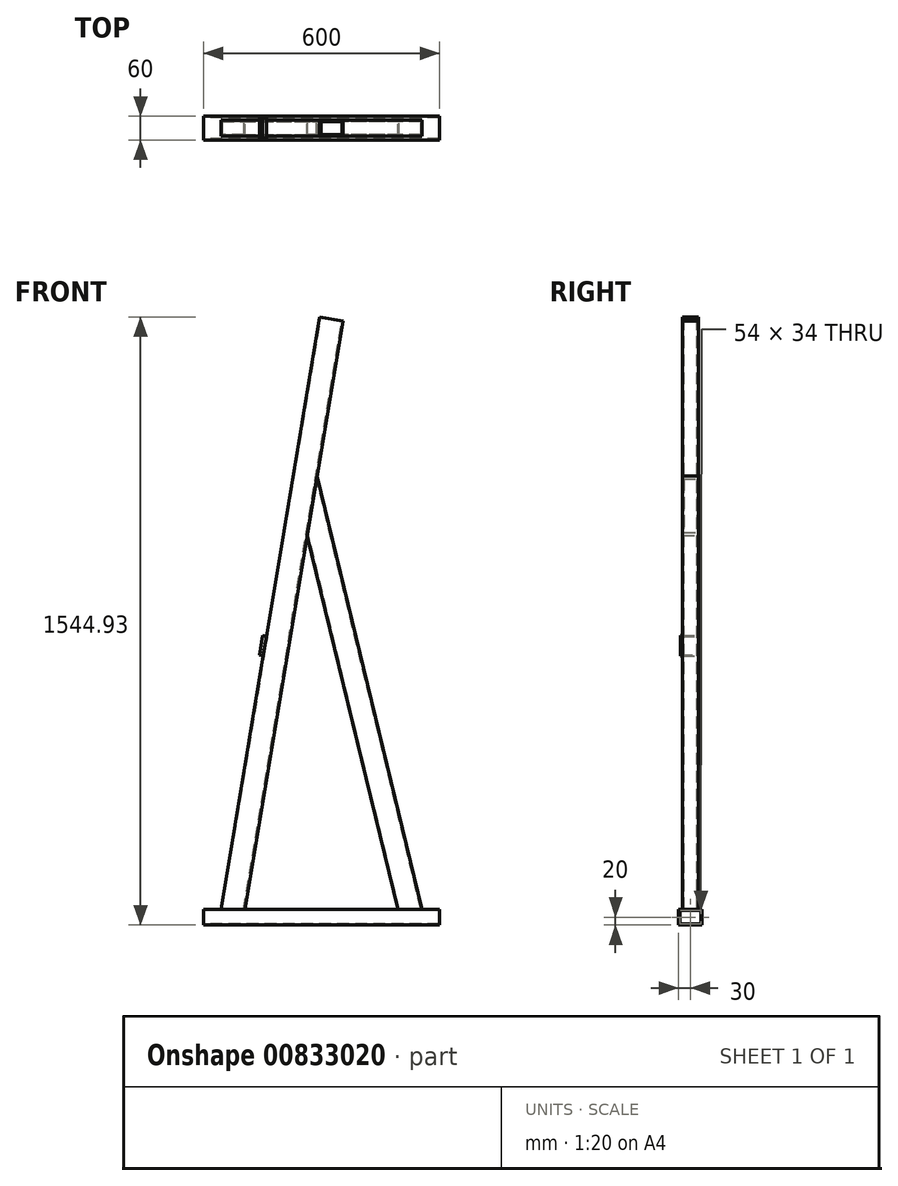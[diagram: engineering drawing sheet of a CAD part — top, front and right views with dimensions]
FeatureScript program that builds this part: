
annotation { "Feature Type Name" : "Feature", "Feature Type Description" : "" }
export const myFeature = defineFeature(function(context is Context, id is Id, definition is map)
    precondition{}
    {
        {
            var Q0;
            Q0=qCreatedBy(makeId("Front.planeOp"),FACE);
            var sketch = newSketch(context, id + "F0", { "sketchPlane" : qUnion([Q0])});
            skLineSegment(sketch, "E0", {"start": v(75, 0) * mm, "end": v(325, 1500) * mm});
            skLineSegment(sketch, "E1", {"start": v(258.33, 1100) * mm, "end": v(525, 0) * mm});
            skLineSegment(sketch, "E2", {"start": v(0, 0) * mm, "end": v(600, 0) * mm});
            skPoint(sketch, "E3", {"position": v(391.67, 550) * mm});
            skSolve(sketch);
        }
        {
            var Q0;
            Q0=sQuery(id+"F0.wireOp",EDGE,"E2");
            var Q1;
            Q1=sQuery(id+"F0.wireOp",VERTEX,"E2.end");
            cPlane(context, id + "F1", {"entities" : qUnion([Q0, Q1]), "cplaneType" : CPlaneType.LINE_POINT, "offset" : 25 * mm, "width" : 150 * mm, "height" : 150 * mm});
        }
        {
            var Q0;
            Q0=qCreatedBy(id+"F1.planeOp",FACE);
            var sketch = newSketch(context, id + "F2", { "sketchPlane" : qUnion([Q0])});
            skLineSegment(sketch, "E4.bottom", {"start": v(-30, 0) * mm, "end": v(30, 0) * mm});
            skLineSegment(sketch, "E4.top", {"start": v(-30, -40) * mm, "end": v(30, -40) * mm});
            skLineSegment(sketch, "E4.left", {"start": v(-30, 0) * mm, "end": v(-30, -40) * mm});
            skLineSegment(sketch, "E4.right", {"start": v(30, 0) * mm, "end": v(30, -40) * mm});
            skLineSegment(sketch, "E5", {"start": v(0, 0) * mm, "end": v(0, -40) * mm, "construction": true});
            skLineSegment(sketch, "E6", {"start": v(30, -20) * mm, "end": v(-30, -20) * mm, "construction": true});
            skLineSegment(sketch, "E7.bottom", {"start": v(27, -3) * mm, "end": v(-27, -3) * mm});
            skLineSegment(sketch, "E7.top", {"start": v(27, -37) * mm, "end": v(-27, -37) * mm});
            skLineSegment(sketch, "E7.left", {"start": v(27, -3) * mm, "end": v(27, -37) * mm});
            skLineSegment(sketch, "E7.right", {"start": v(-27, -3) * mm, "end": v(-27, -37) * mm});
            skSolve(sketch);
        }
        {
            var Q0;
            Q0=makeQuery(id+"F2.imprint","IMPRINT",FACE,{"disambiguationData":[TD([[makeQuery(id+"F2.imprint","IMPRINT",EDGE,{"derivedFrom":sQuery(id+"F2.wireOp",EDGE,"E4.bottom")}),-1.0]])]});
            var Q1;
            Q1=sQuery(id+"F0.wireOp",EDGE,"E2");
            sweep(context, id + "F3", {"profiles" : qUnion([Q0]), "path" : qUnion([Q1])});
        }
        {
            var Q0;
            Q0=sQuery(id+"F0.wireOp",EDGE,"E0");
            var Q1;
            Q1=sQuery(id+"F0.wireOp",VERTEX,"E0.end");
            cPlane(context, id + "F4", {"entities" : qUnion([Q0, Q1]), "cplaneType" : CPlaneType.LINE_POINT, "offset" : 25 * mm, "width" : 150 * mm, "height" : 150 * mm});
        }
        {
            var Q0;
            Q0=qCreatedBy(id+"F4.planeOp",FACE);
            var sketch = newSketch(context, id + "F5", { "sketchPlane" : qUnion([Q0])});
            skPoint(sketch, "E8.0", {"position": v(73.98, 0) * mm});
            skLineSegment(sketch, "E9.bottom", {"start": v(103.98, 20) * mm, "end": v(43.98, 20) * mm});
            skLineSegment(sketch, "E9.top", {"start": v(103.98, -20) * mm, "end": v(43.98, -20) * mm});
            skLineSegment(sketch, "E9.left", {"start": v(103.98, 20) * mm, "end": v(103.98, -20) * mm});
            skLineSegment(sketch, "E9.right", {"start": v(43.98, 20) * mm, "end": v(43.98, -20) * mm});
            skLineSegment(sketch, "E10.bottom", {"start": v(46.98, -17) * mm, "end": v(100.98, -17) * mm});
            skLineSegment(sketch, "E10.top", {"start": v(46.98, 17) * mm, "end": v(100.98, 17) * mm});
            skLineSegment(sketch, "E10.left", {"start": v(46.98, -17) * mm, "end": v(46.98, 17) * mm});
            skLineSegment(sketch, "E10.right", {"start": v(100.98, -17) * mm, "end": v(100.98, 17) * mm});
            skSolve(sketch);
        }
        {
            var Q0;
            Q0=makeQuery(id+"F5.imprint","IMPRINT",FACE,{"disambiguationData":[TD([[makeQuery(id+"F5.imprint","IMPRINT",EDGE,{"derivedFrom":sQuery(id+"F5.wireOp",EDGE,"E9.bottom")}),1.0]])]});
            var Q1;
            Q1=makeQuery(id+"F3.opSweep","SWEPT_BODY",BODY,{"disambiguationData":[OSD([sQuery(id+"F0.wireOp",EDGE,"E2"),sQuery(id+"F2.wireOp",EDGE,"E4.bottom"),sQuery(id+"F2.wireOp",EDGE,"E4.top"),sQuery(id+"F2.wireOp",EDGE,"E4.left"),sQuery(id+"F2.wireOp",EDGE,"E4.right"),sQuery(id+"F2.wireOp",EDGE,"E7.bottom"),sQuery(id+"F2.wireOp",EDGE,"E7.top"),sQuery(id+"F2.wireOp",EDGE,"E7.left"),sQuery(id+"F2.wireOp",EDGE,"E7.right")])]});
            extrude(context, id + "F6", {"entities" : qUnion([Q0]), "endBound" : BoundingType.UP_TO_BODY, "oppositeDirection" : true, "depth" : 25 * mm, "endBoundEntityBody" : qUnion([Q1]), "offsetDistance" : 25 * mm});
        }
        {
            var Q0;
            Q0=sQuery(id+"F0.wireOp",EDGE,"E1");
            var Q1;
            Q1=sQuery(id+"F0.wireOp",VERTEX,"E3");
            cPlane(context, id + "F7", {"entities" : qUnion([Q0, Q1]), "cplaneType" : CPlaneType.LINE_POINT, "offset" : 25 * mm, "width" : 150 * mm, "height" : 150 * mm});
        }
        {
            var Q0;
            Q0=qCreatedBy(id+"F7.planeOp",FACE);
            var sketch = newSketch(context, id + "F8", { "sketchPlane" : qUnion([Q0])});
            skPoint(sketch, "E11.0", {"position": v(510.22, 0) * mm});
            skLineSegment(sketch, "E12.bottom", {"start": v(480.22, -20) * mm, "end": v(540.22, -20) * mm});
            skLineSegment(sketch, "E12.top", {"start": v(480.22, 20) * mm, "end": v(540.22, 20) * mm});
            skLineSegment(sketch, "E12.left", {"start": v(480.22, -20) * mm, "end": v(480.22, 20) * mm});
            skLineSegment(sketch, "E12.right", {"start": v(540.22, -20) * mm, "end": v(540.22, 20) * mm});
            skLineSegment(sketch, "E13.bottom", {"start": v(483.22, -17) * mm, "end": v(537.22, -17) * mm});
            skLineSegment(sketch, "E13.top", {"start": v(483.22, 17) * mm, "end": v(537.22, 17) * mm});
            skLineSegment(sketch, "E13.left", {"start": v(483.22, -17) * mm, "end": v(483.22, 17) * mm});
            skLineSegment(sketch, "E13.right", {"start": v(537.22, -17) * mm, "end": v(537.22, 17) * mm});
            skSolve(sketch);
        }
        {
            var Q0;
            Q0=makeQuery(id+"F8.imprint","IMPRINT",FACE,{"disambiguationData":[TD([[makeQuery(id+"F8.imprint","IMPRINT",EDGE,{"derivedFrom":sQuery(id+"F8.wireOp",EDGE,"E12.bottom")}),1.0]])]});
            var Q1;
            Q1=makeQuery(id+"F3.opSweep","SWEPT_BODY",BODY,{"disambiguationData":[OSD([sQuery(id+"F0.wireOp",EDGE,"E2"),sQuery(id+"F2.wireOp",EDGE,"E4.bottom"),sQuery(id+"F2.wireOp",EDGE,"E4.top"),sQuery(id+"F2.wireOp",EDGE,"E4.left"),sQuery(id+"F2.wireOp",EDGE,"E4.right"),sQuery(id+"F2.wireOp",EDGE,"E7.bottom"),sQuery(id+"F2.wireOp",EDGE,"E7.top"),sQuery(id+"F2.wireOp",EDGE,"E7.left"),sQuery(id+"F2.wireOp",EDGE,"E7.right")])]});
            var Q2;
            Q2=makeQuery(id+"F6.opExtrude","SWEPT_BODY",BODY,{"disambiguationData":[OSD([sQuery(id+"F5.wireOp",EDGE,"E9.bottom"),sQuery(id+"F5.wireOp",EDGE,"E9.top"),sQuery(id+"F5.wireOp",EDGE,"E9.left"),sQuery(id+"F5.wireOp",EDGE,"E9.right"),sQuery(id+"F5.wireOp",EDGE,"E10.bottom"),sQuery(id+"F5.wireOp",EDGE,"E10.top"),sQuery(id+"F5.wireOp",EDGE,"E10.left"),sQuery(id+"F5.wireOp",EDGE,"E10.right")])]});
            extrude(context, id + "F9", {"entities" : qUnion([Q0]), "endBound" : BoundingType.UP_TO_BODY, "depth" : 25 * mm, "endBoundEntityBody" : qUnion([Q1]), "offsetDistance" : 25 * mm, "hasSecondDirection" : true, "secondDirectionBound" : SecondDirectionBoundingType.UP_TO_BODY, "secondDirectionOppositeDirection" : true, "secondDirectionDepth" : 25 * mm, "secondDirectionBoundEntityBody" : qUnion([Q2])});
        }
        {
            var Q0;
            Q0=makeQuery(id+"F6.opExtrude","SWEPT_FACE",FACE,{"disambiguationData":[OSD([sQuery(id+"F5.wireOp",EDGE,"E9.right")])]});
            cPlane(context, id + "F10", {"entities" : qUnion([Q0]), "cplaneType" : CPlaneType.OFFSET, "offset" : 0 * mm, "width" : 150 * mm, "height" : 150 * mm});
        }
        {
            var Q0;
            Q0=qCreatedBy(id+"F10.planeOp",FACE);
            var sketch = newSketch(context, id + "F11", { "sketchPlane" : qUnion([Q0])});
            skLineSegment(sketch, "E14.bottom", {"start": v(25, 660.54) * mm, "end": v(-25, 660.54) * mm});
            skLineSegment(sketch, "E14.top", {"start": v(25, 710.54) * mm, "end": v(-25, 710.54) * mm});
            skLineSegment(sketch, "E14.left", {"start": v(25, 660.54) * mm, "end": v(25, 710.54) * mm});
            skLineSegment(sketch, "E14.right", {"start": v(-25, 660.54) * mm, "end": v(-25, 710.54) * mm});
            skPoint(sketch, "E14.middle", {"position": v(0, 685.54) * mm});
            skLineSegment(sketch, "E15.0.0", {"start": v(-20, 7.33) * mm, "end": v(20, 7.33) * mm});
            skLineSegment(sketch, "E15.0.1", {"start": v(20, 7.33) * mm, "end": v(20, 1533.02) * mm});
            skLineSegment(sketch, "E15.0.2", {"start": v(20, 1533.02) * mm, "end": v(-20, 1533.02) * mm});
            skLineSegment(sketch, "E15.0.3", {"start": v(-20, 1533.02) * mm, "end": v(-20, 7.33) * mm});
            skLineSegment(sketch, "E16", {"start": v(0, 710.54) * mm, "end": v(0, 660.54) * mm, "construction": true});
            skSolve(sketch);
        }
        {
            var Q0;
            {var subQ0=sQuery(id+"F11.wireOp",EDGE,"E15.0.1");var subQ1=sQuery(id+"F11.wireOp",EDGE,"E14.bottom");var subQ2=makeQuery(id+"F11.imprint","INTERSECT",VERTEX,{"derivedFrom":[subQ1,subQ0]});Q0=makeQuery(id+"F11.imprint","IMPRINT",FACE,{"disambiguationData":[TD([[makeQuery(id+"F11.imprint","IMPRINT",EDGE,{"disambiguationData":[TD([[subQ2,-1.0]])],"derivedFrom":subQ1}),-1.0]])]});}
            var Q1;
            {var subQ0=sQuery(id+"F11.wireOp",EDGE,"E14.left");Q1=makeQuery(id+"F11.imprint","IMPRINT",FACE,{"disambiguationData":[TD([[makeQuery(id+"F11.imprint","IMPRINT",EDGE,{"derivedFrom":subQ0}),1.0]])]});}
            var Q2;
            {var subQ0=sQuery(id+"F11.wireOp",EDGE,"E14.right");Q2=makeQuery(id+"F11.imprint","IMPRINT",FACE,{"disambiguationData":[TD([[makeQuery(id+"F11.imprint","IMPRINT",EDGE,{"derivedFrom":subQ0}),-1.0]])]});}
            extrude(context, id + "F12", {"entities" : qUnion([Q0, Q1, Q2]), "operationType" : NewBodyOperationType.ADD, "depth" : 10 * mm, "offsetDistance" : 25 * mm});
        }
    });
